# Revit family: Shower-Bath_and_Shower_Trim-KOHLER-Honesty-K-T99763_1
name_source: partatom
category: Plumbing Fixtures
revit_build: Autodesk Revit 2015 (Build: 20140606_1530(x64)
units: mm (PartAtom-declared; Revit-internal decimal feet)

## types (2) — shared parameters
ADA Compliant = No
Assembly Code = D2010
CW Connection = No
Cold Water Inlet = Cold Water Inlet
Date Modified = 03/08/2019
Default Elevation = 48"
Drain Included = No
Finish = Kohler-Metal-CP-Polished_Chrome
HW Connection = Yes
Handle Clearance = 3 3/16"
Height = 6 1/2"
Hot Water Inlet 1 = Tempered Water Inlet 1
Hot Water Inlet 2 = Tempered Water Inlet 2
Manufacturer = KOHLER Co.
MasterFormat 1995 = 15410
MasterFormat 2004 = 22.41.39
Material = Premium Metal Construction
Product Documentation Link = https://www.us.kohler.com
Product Name = Honesty
Product Page URL = http://www.us.kohler.com
Spout Reach = 6 5/8"
URL = https://www.us.kohler.com
Vent Connection = No
Waste Connection = No
Waste Water Outlet = Waste Water Outlet
Width = 6 1/2"

## per-type parameters (varying)
| type | Description | Distance | Flow Rate | Length | Model | Pressure | Shower_Arm | Shower_Head | Type | WaterSense Certified |
| With Shower Head, CP-Polished Chrome | Rite-Temp(r) pressure-balancing bath and shower trim set, valve not included | 4 1/8" | 2 GPM | 7 1/2" | K-T99763-4-CP | 45.00 psi | No | Yes | 1 | Yes |
| Without Shower Head, CP-Polished Chrome | Rite-Temp(r) bath and shower trim set, less showerhead | 1 11/16" | 0 GPM | 4 3/8" | K-T99763-4L-CP | 0.00 psi | Yes | No | 2 | No |

## geometry (parser evidence)
native form markers: Sweep x9
no freeform markers — native parametric forms only
